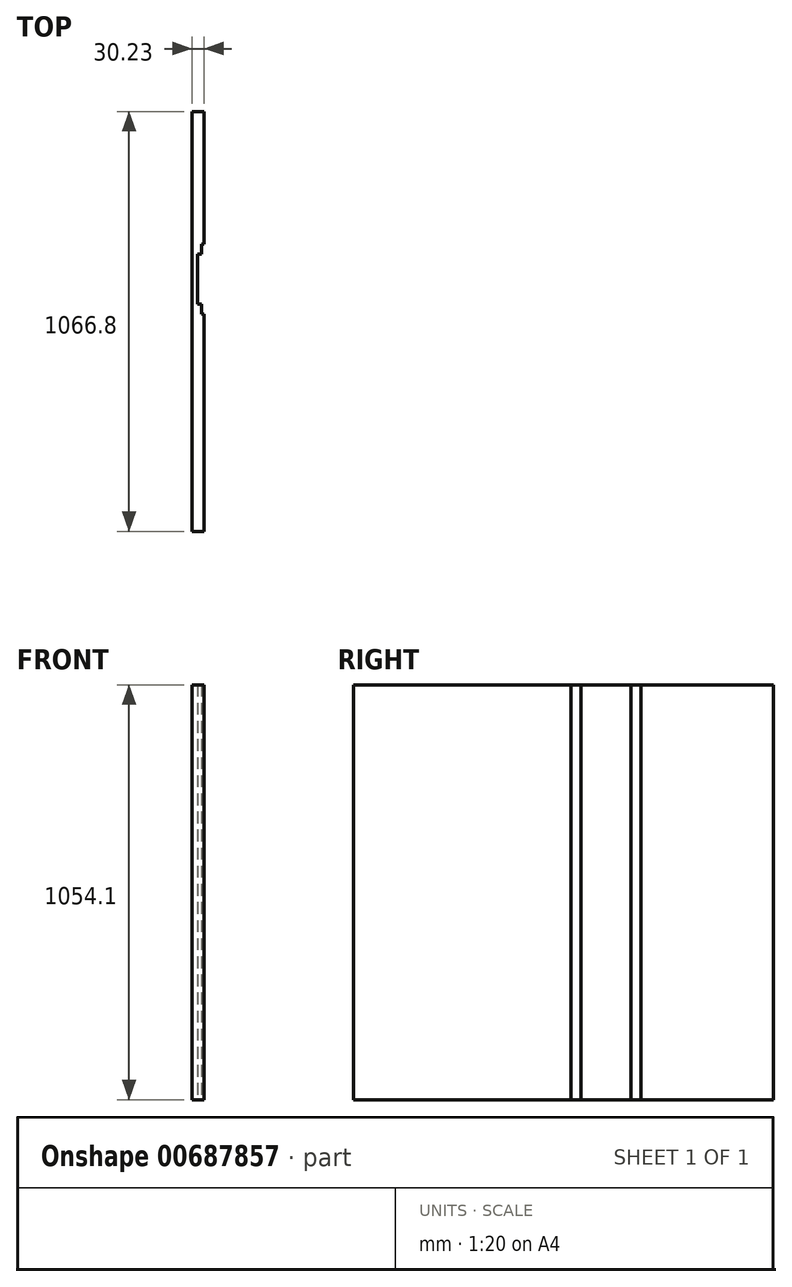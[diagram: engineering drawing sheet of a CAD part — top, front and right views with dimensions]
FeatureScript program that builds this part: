
annotation { "Feature Type Name" : "Feature", "Feature Type Description" : "" }
export const myFeature = defineFeature(function(context is Context, id is Id, definition is map)
    precondition{}
    {
        {
            var Q0;
            Q0=qCreatedBy(makeId("Right.planeOp"),FACE);
            var sketch = newSketch(context, id + "F0", { "sketchPlane" : qUnion([Q0])});
            skLineSegment(sketch, "E0.bottom", {"start": v(533.4, 527.05) * mm, "end": v(-533.4, 527.05) * mm});
            skLineSegment(sketch, "E0.top", {"start": v(533.4, -527.05) * mm, "end": v(-533.4, -527.05) * mm});
            skLineSegment(sketch, "E0.left", {"start": v(533.4, 527.05) * mm, "end": v(533.4, -527.05) * mm});
            skLineSegment(sketch, "E0.right", {"start": v(-533.4, 527.05) * mm, "end": v(-533.4, -527.05) * mm});
            skPoint(sketch, "E0.middle", {"position": v(0, 0) * mm});
            skSolve(sketch);
        }
        {
            var Q0;
            Q0=makeQuery(id+"F0.imprint","IMPRINT",FACE,{"disambiguationData":[TD([[makeQuery(id+"F0.imprint","IMPRINT",EDGE,{"derivedFrom":sQuery(id+"F0.wireOp",EDGE,"E0.bottom")}),1.0]])]});
            extrude(context, id + "F1", {"entities" : qUnion([Q0]), "depth" : 30.23 * mm, "offsetDistance" : 25.4 * mm});
        }
        {
            var Q0;
            Q0=makeQuery(id+"F1.opExtrude","CAP_FACE",FACE,{"disambiguationData":[OSD([sQuery(id+"F0.wireOp",EDGE,"E0.bottom"),sQuery(id+"F0.wireOp",EDGE,"E0.top"),sQuery(id+"F0.wireOp",EDGE,"E0.left"),sQuery(id+"F0.wireOp",EDGE,"E0.right")])],"isStart":false});
            var sketch = newSketch(context, id + "F2", { "sketchPlane" : qUnion([Q0])});
            skLineSegment(sketch, "E1", {"start": v(-533.4, 527.05) * mm, "end": v(19.05, 527.05) * mm});
            skLineSegment(sketch, "E2.bottom", {"start": v(19.05, 527.05) * mm, "end": v(196.85, 527.05) * mm});
            skLineSegment(sketch, "E2.top", {"start": v(19.05, -527.05) * mm, "end": v(196.85, -527.05) * mm});
            skLineSegment(sketch, "E2.left", {"start": v(19.05, 527.05) * mm, "end": v(19.05, -527.05) * mm});
            skLineSegment(sketch, "E2.right", {"start": v(196.85, 527.05) * mm, "end": v(196.85, -527.05) * mm});
            skLineSegment(sketch, "E3.bottom", {"start": v(184.15, 527.05) * mm, "end": v(31.75, 527.05) * mm});
            skLineSegment(sketch, "E3.top", {"start": v(184.15, -527.05) * mm, "end": v(31.75, -527.05) * mm});
            skPoint(sketch, "E3.middle", {"position": v(107.95, 0) * mm});
            skSolve(sketch);
        }
        {
            var Q0;
            {var subQ0=sQuery(id+"F2.wireOp",EDGE,"E2.left");Q0=makeQuery(id+"F2.imprint","IMPRINT",FACE,{"disambiguationData":[TD([[makeQuery(id+"F2.imprint","IMPRINT",EDGE,{"derivedFrom":subQ0}),1.0]])]});}
            extrude(context, id + "F3", {"entities" : qUnion([Q0]), "operationType" : NewBodyOperationType.REMOVE, "oppositeDirection" : true, "depth" : 6.35 * mm, "offsetDistance" : 25.4 * mm});
        }
        {
            var Q0;
            Q0=makeQuery(id+"F3.boolean.opBoolean","COPY",FACE,{"derivedFrom":makeQuery(id+"F3.opExtrude","CAP_FACE",FACE,{"disambiguationData":[OSD([sQuery(id+"F2.wireOp",EDGE,"E2.bottom"),sQuery(id+"F2.wireOp",EDGE,"E2.top"),sQuery(id+"F2.wireOp",EDGE,"E2.left"),sQuery(id+"F2.wireOp",EDGE,"E2.right"),sQuery(id+"F2.wireOp",EDGE,"E3.bottom"),sQuery(id+"F2.wireOp",EDGE,"E3.top")])],"isStart":false})});
            var sketch = newSketch(context, id + "F4", { "sketchPlane" : qUnion([Q0])});
            skLineSegment(sketch, "E4", {"start": v(196.85, 0) * mm, "end": v(19.05, 0) * mm});
            skLineSegment(sketch, "E5.bottom", {"start": v(171.45, 527.05) * mm, "end": v(44.45, 527.05) * mm});
            skLineSegment(sketch, "E5.top", {"start": v(171.45, -527.05) * mm, "end": v(44.45, -527.05) * mm});
            skLineSegment(sketch, "E5.left", {"start": v(171.45, 527.05) * mm, "end": v(171.45, -527.05) * mm});
            skLineSegment(sketch, "E5.right", {"start": v(44.45, 527.05) * mm, "end": v(44.45, -527.05) * mm});
            skPoint(sketch, "E5.middle", {"position": v(107.95, 0) * mm});
            skSolve(sketch);
        }
        {
            var Q0;
            {var subQ5=sQuery(id+"F4.wireOp",EDGE,"E5.top");Q0=makeQuery(id+"F4.imprint","IMPRINT",FACE,{"disambiguationData":[TD([[makeQuery(id+"F4.imprint","IMPRINT",EDGE,{"derivedFrom":subQ5}),-1.0]])]});}
            var Q1;
            {var subQ5=sQuery(id+"F4.wireOp",EDGE,"E5.bottom");Q1=makeQuery(id+"F4.imprint","IMPRINT",FACE,{"disambiguationData":[TD([[makeQuery(id+"F4.imprint","IMPRINT",EDGE,{"derivedFrom":subQ5}),1.0]])]});}
            extrude(context, id + "F5", {"entities" : qUnion([Q0, Q1]), "operationType" : NewBodyOperationType.REMOVE, "oppositeDirection" : true, "depth" : 9.52 * mm, "offsetDistance" : 25.4 * mm});
        }
    });
